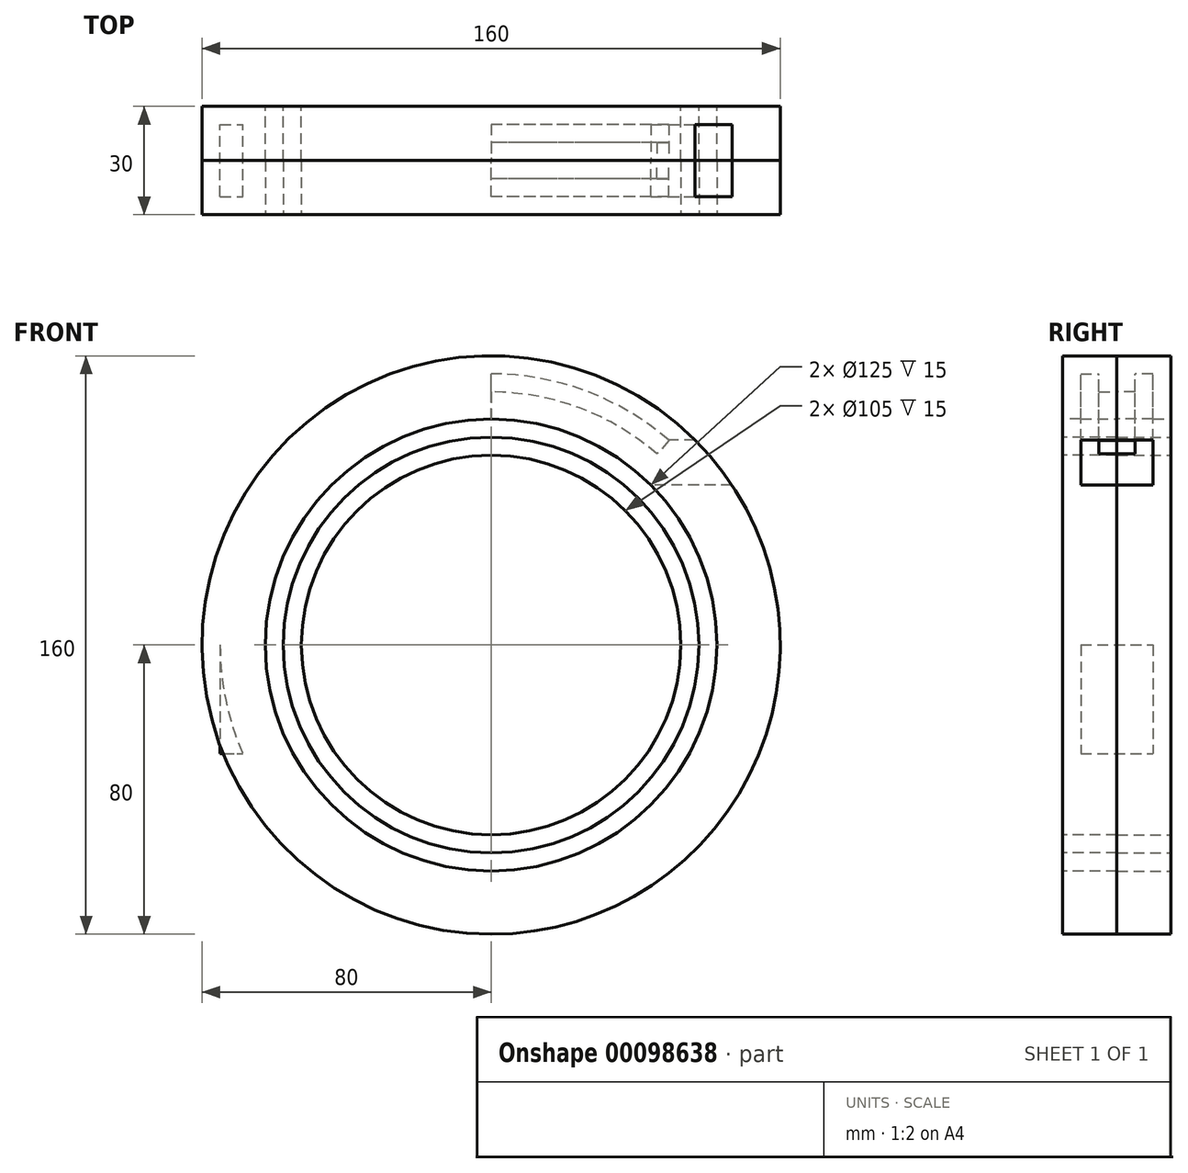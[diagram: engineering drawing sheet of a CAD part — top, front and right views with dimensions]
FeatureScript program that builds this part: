
annotation { "Feature Type Name" : "Feature", "Feature Type Description" : "" }
export const myFeature = defineFeature(function(context is Context, id is Id, definition is map)
    precondition{}
    {
        {
            var Q0;
            Q0=qCreatedBy(makeId("Front.planeOp"),FACE);
            var sketch = newSketch(context, id + "F0", { "sketchPlane" : qUnion([Q0])});
            skCircle(sketch, "E0", {"center": v(0, 0) * mm, "radius": 62.5 * mm});
            skCircle(sketch, "E1", {"center": v(0, 0) * mm, "radius": 75 * mm});
            skLineSegment(sketch, "E2", {"start": v(-62.5, 0) * mm, "end": v(-75, 0) * mm});
            skLineSegment(sketch, "E3", {"start": v(0, 0) * mm, "end": v(53.03, 53.03) * mm});
            skLineSegment(sketch, "E4.bottom", {"start": v(-75, 0) * mm, "end": v(-62.5, 0) * mm});
            skLineSegment(sketch, "E4.top", {"start": v(-75, -30) * mm, "end": v(-62.5, -30) * mm});
            skLineSegment(sketch, "E4.left", {"start": v(-75, 0) * mm, "end": v(-75, -30) * mm});
            skLineSegment(sketch, "E4.right", {"start": v(-62.5, 0) * mm, "end": v(-62.5, -30) * mm});
            skLineSegment(sketch, "E5.left", {"start": v(0, 62.5) * mm, "end": v(0, 75) * mm});
            skLineSegment(sketch, "E6.bottom", {"start": v(44.2, 44.2) * mm, "end": v(79.2, 44.2) * mm});
            skLineSegment(sketch, "E6.top", {"start": v(44.2, 56.7) * mm, "end": v(79.2, 56.7) * mm});
            skLineSegment(sketch, "E6.left", {"start": v(44.2, 44.2) * mm, "end": v(44.2, 56.7) * mm});
            skLineSegment(sketch, "E6.right", {"start": v(79.2, 44.2) * mm, "end": v(79.2, 56.7) * mm});
            skSolve(sketch);
        }
        {
            var Q0;
            {var subQ0=sQuery(id+"F0.wireOp",EDGE,"E4.bottom");Q0=makeQuery(id+"F0.imprint","IMPRINT",FACE,{"disambiguationData":[TD([[makeQuery(id+"F0.imprint","IMPRINT",EDGE,{"derivedFrom":subQ0}),-1.0]])]});}
            var Q1;
            {var subQ0=sQuery(id+"F0.wireOp",EDGE,"E4.left");Q1=makeQuery(id+"F0.imprint","IMPRINT",FACE,{"disambiguationData":[TD([[makeQuery(id+"F0.imprint","IMPRINT",EDGE,{"derivedFrom":subQ0}),1.0]])]});}
            var Q2;
            {var subQ0=sQuery(id+"F0.wireOp",EDGE,"E4.bottom");Q2=makeQuery(id+"F0.imprint","IMPRINT",FACE,{"disambiguationData":[TD([[makeQuery(id+"F0.imprint","IMPRINT",EDGE,{"derivedFrom":subQ0}),1.0]])]});}
            var Q3;
            {var subQ0=sQuery(id+"F0.wireOp",EDGE,"E5.left");Q3=makeQuery(id+"F0.imprint","IMPRINT",FACE,{"disambiguationData":[TD([[makeQuery(id+"F0.imprint","IMPRINT",EDGE,{"derivedFrom":subQ0}),-1.0]])]});}
            var Q4;
            {var subQ3=sQuery(id+"F0.wireOp",EDGE,"E3");var subQ5=sQuery(id+"F0.wireOp",EDGE,"E1");var subQ6=makeQuery(id+"F0.imprint","INTERSECT",VERTEX,{"derivedFrom":[subQ5,subQ3]});Q4=makeQuery(id+"F0.imprint","IMPRINT",FACE,{"disambiguationData":[TD([[makeQuery(id+"F0.imprint","IMPRINT",EDGE,{"disambiguationData":[TD([[subQ6,-1.0]])],"derivedFrom":subQ5}),1.0]])]});}
            var Q5;
            {var subQ0=sQuery(id+"F0.wireOp",EDGE,"E5.top");Q5=makeQuery(id+"F0.imprint","IMPRINT",FACE,{"disambiguationData":[TD([[makeQuery(id+"F0.imprint","IMPRINT",EDGE,{"derivedFrom":subQ0}),-1.0]])]});}
            var Q6;
            {var subQ0=sQuery(id+"F0.wireOp",EDGE,"E6.right");Q6=makeQuery(id+"F0.imprint","IMPRINT",FACE,{"disambiguationData":[TD([[makeQuery(id+"F0.imprint","IMPRINT",EDGE,{"derivedFrom":subQ0}),1.0]])]});}
            var Q7;
            {var subQ0=sQuery(id+"F0.wireOp",EDGE,"E3");var subQ1=sQuery(id+"F0.wireOp",EDGE,"E1");var subQ2=makeQuery(id+"F0.imprint","INTERSECT",VERTEX,{"derivedFrom":[subQ1,subQ0]});Q7=makeQuery(id+"F0.imprint","IMPRINT",FACE,{"disambiguationData":[TD([[makeQuery(id+"F0.imprint","IMPRINT",EDGE,{"disambiguationData":[TD([[subQ2,1.0]])],"derivedFrom":subQ1}),1.0]])]});}
            extrude(context, id + "F1", {"entities" : qUnion([Q0, Q1, Q2, Q3, Q4, Q5, Q6, Q7]), "endBound" : BoundingType.SYMMETRIC, "depth" : 20 * mm});
        }
        {
            var Q0;
            Q0=qCreatedBy(makeId("Front.planeOp"),FACE);
            var sketch = newSketch(context, id + "F2", { "sketchPlane" : qUnion([Q0])});
            skCircle(sketch, "E7", {"center": v(0, 0) * mm, "radius": 75 * mm});
            skCircle(sketch, "E8", {"center": v(0, 0) * mm, "radius": 70 * mm});
            skLineSegment(sketch, "E9", {"start": v(0, 0) * mm, "end": v(49.2, 56.6) * mm});
            skLineSegment(sketch, "E10", {"start": v(0, 0) * mm, "end": v(-75, 0) * mm});
            skSolve(sketch);
        }
        {
            var Q0;
            {var subQ0=sQuery(id+"F2.wireOp",EDGE,"E9");var subQ1=sQuery(id+"F2.wireOp",EDGE,"E7");var subQ2=makeQuery(id+"F2.imprint","INTERSECT",VERTEX,{"derivedFrom":[subQ1,subQ0]});Q0=makeQuery(id+"F2.imprint","IMPRINT",FACE,{"disambiguationData":[TD([[makeQuery(id+"F2.imprint","IMPRINT",EDGE,{"disambiguationData":[TD([[subQ2,-1.0]])],"derivedFrom":subQ1}),1.0]])]});}
            extrude(context, id + "F3", {"entities" : qUnion([Q0]), "operationType" : NewBodyOperationType.REMOVE, "endBound" : BoundingType.SYMMETRIC, "depth" : 10 * mm});
        }
        {
            var Q0;
            Q0=qCreatedBy(makeId("Front.planeOp"),FACE);
            var sketch = newSketch(context, id + "F4", { "sketchPlane" : qUnion([Q0])});
            skCircle(sketch, "E11", {"center": v(0, 0) * mm, "radius": 57.5 * mm});
            skCircle(sketch, "E12", {"center": v(0, 0) * mm, "radius": 80 * mm});
            skLineSegment(sketch, "E13", {"start": v(0, 0) * mm, "end": v(0, 80) * mm});
            skLineSegment(sketch, "E14", {"start": v(0, 80) * mm, "end": v(0, 0) * mm});
            skLineSegment(sketch, "E15", {"start": v(0, 0) * mm, "end": v(-78.78, 13.9) * mm});
            skSolve(sketch);
        }
        {
            var Q0;
            {var subQ0=sQuery(id+"F4.wireOp",EDGE,"E14");var subQ1=sQuery(id+"F4.wireOp",EDGE,"E11");var subQ2=makeQuery(id+"F4.imprint","INTERSECT",VERTEX,{"derivedFrom":[subQ1,subQ0]});Q0=makeQuery(id+"F4.imprint","IMPRINT",FACE,{"disambiguationData":[TD([[makeQuery(id+"F4.imprint","IMPRINT",EDGE,{"disambiguationData":[TD([[subQ2,-1.0]])],"derivedFrom":subQ1}),-1.0]])]});}
            extrude(context, id + "F5", {"entities" : qUnion([Q0]), "depth" : 15 * mm});
        }
        {
            var Q0;
            Q0=makeQuery(id+"F1.opExtrude","SWEPT_BODY",BODY,{"disambiguationData":[OSD([sQuery(id+"F0.wireOp",EDGE,"E0"),sQuery(id+"F0.wireOp",EDGE,"E1"),sQuery(id+"F0.wireOp",EDGE,"E4.top"),sQuery(id+"F0.wireOp",EDGE,"E4.left"),sQuery(id+"F0.wireOp",EDGE,"E4.right"),sQuery(id+"F0.wireOp",EDGE,"E6.bottom"),sQuery(id+"F0.wireOp",EDGE,"E6.top"),sQuery(id+"F0.wireOp",EDGE,"E6.right")])]});
            var Q1;
            Q1=makeQuery(id+"F5.opExtrude","SWEPT_BODY",BODY,{"disambiguationData":[OSD([sQuery(id+"F4.wireOp",EDGE,"E11"),sQuery(id+"F4.wireOp",EDGE,"E12"),sQuery(id+"F4.wireOp",EDGE,"E14"),sQuery(id+"F4.wireOp",EDGE,"E15")])]});
            booleanBodies(context, id + "F6", {"operationType" : BooleanOperationType.SUBTRACTION, "tools" : qUnion([Q0]), "targets" : qUnion([Q1])});
        }
        {
            var Q0;
            Q0=makeQuery(id+"F5.opExtrude","CAP_FACE",FACE,{"disambiguationData":[OSD([sQuery(id+"F4.wireOp",EDGE,"E11"),sQuery(id+"F4.wireOp",EDGE,"E12"),sQuery(id+"F4.wireOp",EDGE,"E14"),sQuery(id+"F4.wireOp",EDGE,"E15")])],"isStart":false});
            var sketch = newSketch(context, id + "F7", { "sketchPlane" : qUnion([Q0])});
            skCircle(sketch, "E16", {"center": v(0, 0) * mm, "radius": 57.5 * mm});
            skCircle(sketch, "E17", {"center": v(0, 0) * mm, "radius": 52.5 * mm});
            skCircle(sketch, "E18", {"center": v(0, 0) * mm, "radius": 62.5 * mm});
            skLineSegment(sketch, "E19", {"start": v(0, 0) * mm, "end": v(-69.28, 40) * mm});
            skLineSegment(sketch, "E20", {"start": v(-69.28, 40) * mm, "end": v(0, 0) * mm});
            skLineSegment(sketch, "E21", {"start": v(0, 0) * mm, "end": v(-27.36, 75.18) * mm});
            skLineSegment(sketch, "E22", {"start": v(0, 0) * mm, "end": v(-17.23, 60.08) * mm});
            skLineSegment(sketch, "E23", {"start": v(-17.23, 60.08) * mm, "end": v(0, 0) * mm});
            skLineSegment(sketch, "E24", {"start": v(0, 0) * mm, "end": v(-12.34, 61.27) * mm});
            skLineSegment(sketch, "E25", {"start": v(-12.34, 61.27) * mm, "end": v(0, 0) * mm});
            skLineSegment(sketch, "E26", {"start": v(0, 0) * mm, "end": v(-8.04, 61.98) * mm});
            skLineSegment(sketch, "E27", {"start": v(-8.04, 61.98) * mm, "end": v(0, 0) * mm});
            skLineSegment(sketch, "E28", {"start": v(0, 0) * mm, "end": v(-51.51, 35.4) * mm});
            skLineSegment(sketch, "E29", {"start": v(-51.51, 35.4) * mm, "end": v(0, 0) * mm});
            skLineSegment(sketch, "E30", {"start": v(-48.92, 38.9) * mm, "end": v(0, 0) * mm});
            skLineSegment(sketch, "E31", {"start": v(-46.08, 42.22) * mm, "end": v(0, 0) * mm});
            skLineSegment(sketch, "E32", {"start": v(0, 0) * mm, "end": v(0, 0) * mm});
            skSolve(sketch);
        }
        {
            var Q0;
            {var subQ0=sQuery(id+"F7.wireOp",EDGE,"E29");var subQ1=sQuery(id+"F7.wireOp",EDGE,"E16");var subQ2=makeQuery(id+"F7.imprint","INTERSECT",VERTEX,{"derivedFrom":[subQ1,subQ0]});Q0=makeQuery(id+"F7.imprint","IMPRINT",FACE,{"disambiguationData":[TD([[makeQuery(id+"F7.imprint","IMPRINT",EDGE,{"disambiguationData":[TD([[subQ2,-1.0]])],"derivedFrom":subQ1}),1.0]])]});}
            var Q1;
            {var subQ0=sQuery(id+"F7.wireOp",EDGE,"E23");var subQ1=sQuery(id+"F7.wireOp",EDGE,"E16");var subQ2=makeQuery(id+"F7.imprint","INTERSECT",VERTEX,{"derivedFrom":[subQ1,subQ0]});Q1=makeQuery(id+"F7.imprint","IMPRINT",FACE,{"disambiguationData":[TD([[makeQuery(id+"F7.imprint","IMPRINT",EDGE,{"disambiguationData":[TD([[subQ2,-1.0]])],"derivedFrom":subQ1}),1.0]])]});}
            var Q2;
            {var subQ0=sQuery(id+"F4.wireOp",EDGE,"E11");var subQ1=sQuery(id+"F4.wireOp",EDGE,"E14");var subQ2=sQuery(id+"F4.wireOp",EDGE,"E15");Q2=makeQuery(id+"F6.opBoolean","SPLIT",FACE,{"disambiguationData":[TD([makeQuery(id+"F1.opExtrude","SWEPT_FACE",FACE,{"disambiguationData":[OSD([sQuery(id+"F0.wireOp",EDGE,"E0")])]})])],"derivedFrom":makeQuery(id+"F5.opExtrude","CAP_FACE",FACE,{"disambiguationData":[OSD([subQ0,sQuery(id+"F4.wireOp",EDGE,"E12"),subQ1,subQ2])],"isStart":true})});}
            extrude(context, id + "F8", {"entities" : qUnion([Q0, Q1]), "operationType" : NewBodyOperationType.ADD, "endBound" : BoundingType.UP_TO_SURFACE, "oppositeDirection" : true, "endBoundEntityFace" : qUnion([Q2]), "depth" : 25 * mm});
        }
        {
            var Q0;
            {var subQ0=sQuery(id+"F7.wireOp",EDGE,"E31");var subQ1=sQuery(id+"F7.wireOp",EDGE,"E16");var subQ2=makeQuery(id+"F7.imprint","INTERSECT",VERTEX,{"derivedFrom":[subQ1,subQ0]});Q0=makeQuery(id+"F7.imprint","IMPRINT",FACE,{"disambiguationData":[TD([[makeQuery(id+"F7.imprint","IMPRINT",EDGE,{"disambiguationData":[TD([[subQ2,-1.0]])],"derivedFrom":subQ1}),-1.0]])]});}
            var Q1;
            {var subQ0=sQuery(id+"F7.wireOp",EDGE,"E27");var subQ1=sQuery(id+"F7.wireOp",EDGE,"E16");var subQ2=makeQuery(id+"F7.imprint","INTERSECT",VERTEX,{"derivedFrom":[subQ1,subQ0]});Q1=makeQuery(id+"F7.imprint","IMPRINT",FACE,{"disambiguationData":[TD([[makeQuery(id+"F7.imprint","IMPRINT",EDGE,{"disambiguationData":[TD([[subQ2,-1.0]])],"derivedFrom":subQ1}),-1.0]])]});}
            extrude(context, id + "F9", {"entities" : qUnion([Q0, Q1]), "operationType" : NewBodyOperationType.REMOVE, "oppositeDirection" : true, "depth" : 25 * mm});
        }
        {
            var Q0;
            Q0=makeQuery(id+"F5.opExtrude","SWEPT_BODY",BODY,{"disambiguationData":[OSD([sQuery(id+"F4.wireOp",EDGE,"E11"),sQuery(id+"F4.wireOp",EDGE,"E12"),sQuery(id+"F4.wireOp",EDGE,"E14"),sQuery(id+"F4.wireOp",EDGE,"E15")])]});
            var Q1;
            Q1=qCreatedBy(makeId("Front.planeOp"),FACE);
            mirror(context, id + "F10", {"entities" : qUnion([Q0]), "mirrorPlane" : qUnion([Q1])});
        }
    });
